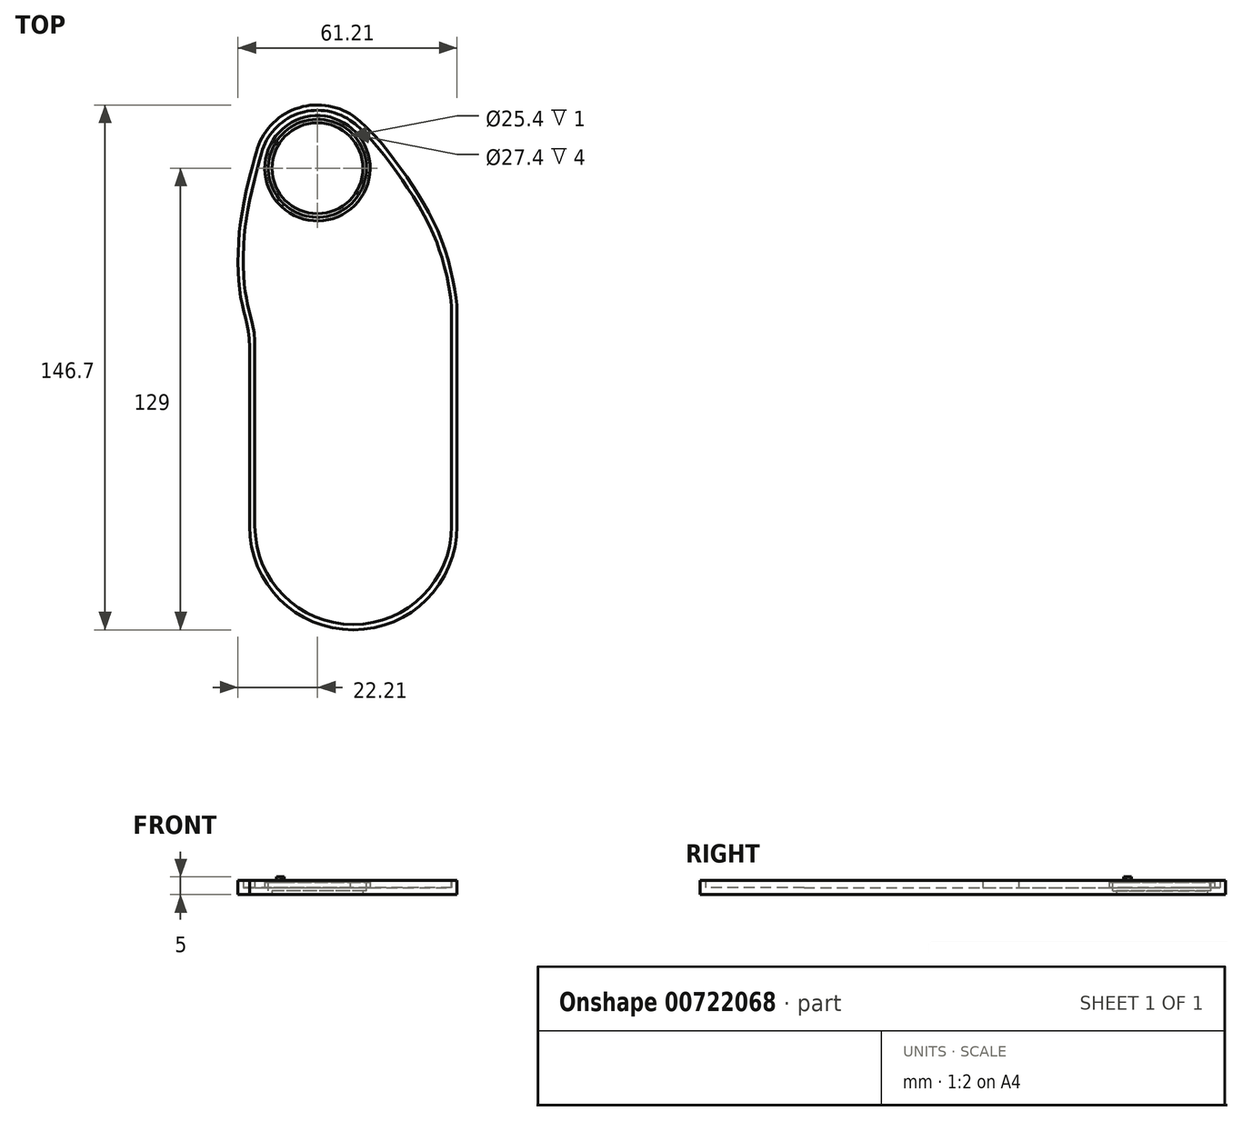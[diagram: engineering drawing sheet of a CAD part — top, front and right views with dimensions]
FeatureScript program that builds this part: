
annotation { "Feature Type Name" : "Feature", "Feature Type Description" : "" }
export const myFeature = defineFeature(function(context is Context, id is Id, definition is map)
    precondition{}
    {
        {
            var Q0;
            Q0=qCreatedBy(makeId("Top.planeOp"),FACE);
            var sketch = newSketch(context, id + "F0", { "sketchPlane" : qUnion([Q0])});
            skArc(sketch, "E0", {"start": v(-29, -45) * mm, "mid": v(0, -74) * mm, "end": v(29, -45) * mm});
            skArc(sketch, "E1", {"start": v(0, 69.6) * mm, "mid": v(-16.14, 71.6) * mm, "end": v(-27.1, 59.59) * mm});
            skLineSegment(sketch, "E2", {"start": v(29, -45) * mm, "end": v(29, 15) * mm});
            skLineSegment(sketch, "E3", {"start": v(-29, -45) * mm, "end": v(-29, 5) * mm});
            skFitSpline(sketch, "E4", {"points": [v(-29, 5) * mm, v(-31.24, 17.94) * mm, v(-31.52, 39.79) * mm, v(-27.1, 59.59) * mm], "startDerivative": vector(0, 58.47) * mm, "endDerivative": vector(9.43, 35.14) * mm});
            skFitSpline(sketch, "E5", {"points": [v(29, 15) * mm, v(25.63, 32.2) * mm, v(14.84, 52.68) * mm, v(0, 69.6) * mm], "startDerivative": vector(0, 34.21) * mm, "endDerivative": vector(-41.86, 28.66) * mm});
            skCircle(sketch, "E6", {"center": v(-10, 55) * mm, "radius": 12.7 * mm});
            skLineSegment(sketch, "E7.0", {"start": v(-27.5, -45) * mm, "end": v(-27.5, 5) * mm});
            skArc(sketch, "E7.1", {"start": v(-0.85, 68.37) * mm, "mid": v(-15.62, 70.2) * mm, "end": v(-25.65, 59.2) * mm});
            skFitSpline(sketch, "E7.2", {"points": [v(27.5, 15) * mm, v(27.5, 15.64) * mm, v(27.4, 17.3) * mm, v(26.97, 20.55) * mm, v(26.26, 24.3) * mm, v(25.45, 27.62) * mm, v(24.69, 30.27) * mm, v(24.05, 32.22) * mm, v(23.37, 34.12) * mm, v(22.37, 36.6) * mm, v(21, 39.61) * mm, v(19.13, 43.14) * mm, v(17.06, 46.62) * mm, v(15.17, 49.54) * mm, v(13.55, 51.9) * mm, v(11.89, 54.3) * mm, v(9.71, 57.28) * mm, v(7.02, 60.7) * mm, v(4.3, 63.81) * mm, v(1.64, 66.46) * mm, v(-0.04, 67.82) * mm, v(-0.85, 68.37) * mm]});
            skFitSpline(sketch, "E7.3", {"points": [v(-27.5, 5) * mm, v(-27.5, 6.27) * mm, v(-27.64, 8.58) * mm, v(-28.15, 11.53) * mm, v(-28.7, 13.74) * mm, v(-29.14, 15.46) * mm, v(-29.46, 16.77) * mm, v(-29.76, 18.13) * mm, v(-30.02, 19.58) * mm, v(-30.24, 21.14) * mm, v(-30.48, 23.33) * mm, v(-30.68, 26.27) * mm, v(-30.74, 30.06) * mm, v(-30.6, 34.01) * mm, v(-30.31, 37.4) * mm, v(-29.97, 40.12) * mm, v(-29.55, 42.84) * mm, v(-28.9, 46.22) * mm, v(-28.04, 50.09) * mm, v(-26.85, 54.83) * mm, v(-26.04, 57.72) * mm, v(-25.65, 59.2) * mm]});
            skLineSegment(sketch, "E7.4", {"start": v(27.5, -45) * mm, "end": v(27.5, 15) * mm});
            skArc(sketch, "E7.5", {"start": v(-27.5, -45) * mm, "mid": v(0, -72.5) * mm, "end": v(27.5, -45) * mm});
            skSolve(sketch);
        }
        {
            var Q0;
            Q0=makeQuery(id+"F0.imprint","IMPRINT",FACE,{"disambiguationData":[TD([[makeQuery(id+"F0.imprint","IMPRINT",EDGE,{"derivedFrom":sQuery(id+"F0.wireOp",EDGE,"E6")}),-1.0]])]});
            extrude(context, id + "F1", {"entities" : qUnion([Q0]), "depth" : 2 * mm, "offsetDistance" : 25.4 * mm});
        }
        {
            var Q0;
            Q0=makeQuery(id+"F1.opExtrude","CAP_FACE",FACE,{"disambiguationData":[OSD([sQuery(id+"F0.wireOp",EDGE,"E0"),sQuery(id+"F0.wireOp",EDGE,"E1"),sQuery(id+"F0.wireOp",EDGE,"E2"),sQuery(id+"F0.wireOp",EDGE,"E3"),sQuery(id+"F0.wireOp",EDGE,"E4"),sQuery(id+"F0.wireOp",EDGE,"E5"),sQuery(id+"F0.wireOp",EDGE,"E6")])],"isStart":false});
            var sketch = newSketch(context, id + "F2", { "sketchPlane" : qUnion([Q0])});
            skCircle(sketch, "E8", {"center": v(-10, 55) * mm, "radius": 13.7 * mm});
            skCircle(sketch, "E9", {"center": v(-10, 55) * mm, "radius": 14.7 * mm});
            skSolve(sketch);
        }
        {
            var Q0;
            Q0=makeQuery(id+"F2.imprint","IMPRINT",FACE,{"disambiguationData":[TD([[makeQuery(id+"F2.imprint","IMPRINT",EDGE,{"derivedFrom":sQuery(id+"F2.wireOp",EDGE,"E8")}),1.0]])]});
            extrude(context, id + "F3", {"entities" : qUnion([Q0]), "operationType" : NewBodyOperationType.REMOVE, "oppositeDirection" : true, "depth" : 1 * mm, "offsetDistance" : 25.4 * mm});
        }
        {
            var Q0;
            Q0=makeQuery(id+"F2.imprint","IMPRINT",FACE,{"disambiguationData":[TD([[makeQuery(id+"F2.imprint","IMPRINT",EDGE,{"derivedFrom":sQuery(id+"F2.wireOp",EDGE,"E8")}),-1.0]])]});
            extrude(context, id + "F4", {"entities" : qUnion([Q0]), "operationType" : NewBodyOperationType.ADD, "depth" : 1.5 * mm, "offsetDistance" : 25.4 * mm});
        }
        {
            var Q0;
            Q0=makeQuery(id+"F4.opExtrude","CAP_FACE",FACE,{"disambiguationData":[OSD([sQuery(id+"F2.wireOp",EDGE,"E8"),sQuery(id+"F2.wireOp",EDGE,"E9")])],"isStart":false});
            var sketch = newSketch(context, id + "F5", { "sketchPlane" : qUnion([Q0])});
            skLineSegment(sketch, "E10", {"start": v(-19.3, 44.95) * mm, "end": v(-20.67, 46.41) * mm});
            skLineSegment(sketch, "E11", {"start": v(-20.67, 46.41) * mm, "end": v(-21.4, 45.73) * mm});
            skLineSegment(sketch, "E12", {"start": v(-19.3, 44.95) * mm, "end": v(-20.04, 44.26) * mm});
            skLineSegment(sketch, "E13", {"start": v(-20.04, 44.26) * mm, "end": v(-21.4, 45.73) * mm});
            skSolve(sketch);
        }
        {
            var Q0;
            {var subQ0=sQuery(id+"F5.wireOp",EDGE,"E11");Q0=makeQuery(id+"F5.imprint","IMPRINT",FACE,{"disambiguationData":[TD([[makeQuery(id+"F5.imprint","IMPRINT",EDGE,{"derivedFrom":subQ0}),1.0]])]});}
            extrude(context, id + "F6", {"entities" : qUnion([Q0]), "operationType" : NewBodyOperationType.ADD, "depth" : 1.5 * mm, "offsetDistance" : 25.4 * mm});
        }
        {
            var Q0;
            Q0=makeQuery(id+"F0.imprint","IMPRINT",FACE,{"disambiguationData":[TD([[makeQuery(id+"F0.imprint","IMPRINT",EDGE,{"derivedFrom":sQuery(id+"F0.wireOp",EDGE,"E0")}),1.0]])]});
            extrude(context, id + "F7", {"entities" : qUnion([Q0]), "operationType" : NewBodyOperationType.ADD, "depth" : 4 * mm, "offsetDistance" : 25.4 * mm});
        }
    });
